# Revit family: Facade_60_Curtain_Wall_S13_Standard
name_source: partatom
category: Windows
revit_build: Autodesk Revit 2014 (Build: 20130308_1515(x64)
units: mm (PartAtom-declared; Revit-internal decimal feet)

## types (72) — shared parameters
100mm Mullion = Yes
160mm Mullion = No
190mm Mullion = No
Custom Offset From Exterior = 10 mm  [stored 0.0328084 ft]
DG Gasket Thickness = 12 mm  [stored 0.0393701 ft]
Description = Curtain wall, S13
Frame Bottom Gap = 30 mm  [stored 0.0984252 ft]
Frame Thickness = 102 mm
Glazing Bottom Gap = 70 mm
Glazing Side Gap = 40 mm  [stored 0.131234 ft]
Glazing Top Gap = 40 mm  [stored 0.131234 ft]
Half Expansion Break = No
Jamb Width = 60 mm  [stored 0.19685 ft]
Limit Door Height Max = 18149 mm
Limit Door Height Min = 1049 mm
Limit Door Width Max = 3080 mm
Limit Door Width Min = 380 mm
Limit Panel Height Max = 6000 mm  [stored 19.685 ft]
Limit Panel Height Min = 300 mm  [stored 0.984252 ft]
Limit Panel Width Max = 3000 mm  [stored 9.84252 ft]
Limit Panel Width Min = 300 mm  [stored 0.984252 ft]
Manufacturer = Crealco
Max System DG Unit Thickness = 25 mm  [stored 0.082021 ft]
Model = Façade 60
Mullion Configuration = 1 mm  [stored 0.00328084 ft]
Quarter Expansion Break = No
Sill Height = 85 mm  [stored 0.278871 ft]
Thermal Break Material = Plastic, Opaque Black
URL = http://www.crealco.co.za
Wall Closure = By host
zero-valued in all types: Default Sill Height

## per-type parameters (varying)
| type | Custom Curtain Wall Height | Custom Curtain Wall Width | Custom Windload | Intruderprufe Insulated LowE SHGC Value | Intruderprufe Insulated LowE U Value | Intruderprufe Insulated SHGC Value | Intruderprufe Insulated U Value | Intruderprufe LowE SHGC Value | Intruderprufe LowE U Value | Intruderprufe SHGC Value | Intruderprufe U Value |
| F60-S13-0925-1000Pa | 2490 mm | 890 mm  [stored 2.91995 ft] | 1000 mm  [stored 3.28084 ft] | 0.491 | 2.76 | 0.544 | 3.31 | 0.553 | 4.63 | 0.63 | 5.75 |
| F60-S13-0925-1500Pa | 2490 mm | 890 mm  [stored 2.91995 ft] | 1500 mm  [stored 4.92126 ft] | 0.491 | 2.76 | 0.544 | 3.31 | 0.553 | 4.63 | 0.63 | 5.75 |
| F60-S13-0925-2000Pa | 2490 mm | 890 mm  [stored 2.91995 ft] | 2000 mm  [stored 6.56168 ft] | 0.491 | 2.76 | 0.544 | 3.31 | 0.553 | 4.63 | 0.63 | 5.75 |
| F60-S13-1225-1000Pa | 2490 mm | 1190 mm  [stored 3.9042 ft] | 1000 mm  [stored 3.28084 ft] | 0.508 | 2.65 | 0.564 | 3.23 | 0.573 | 4.52 | 0.653 | 5.76 |
| F60-S13-1225-1500Pa | 2490 mm | 1190 mm  [stored 3.9042 ft] | 1500 mm  [stored 4.92126 ft] | 0.508 | 2.65 | 0.564 | 3.23 | 0.573 | 4.52 | 0.653 | 5.76 |
| F60-S13-1225-2000Pa | 2490 mm | 1190 mm  [stored 3.9042 ft] | 2000 mm  [stored 6.56168 ft] | 0.508 | 2.65 | 0.564 | 3.23 | 0.573 | 4.52 | 0.653 | 5.76 |
| F60-S13-1525-1000Pa | 2490 mm | 1490 mm  [stored 4.88845 ft] | 1000 mm  [stored 3.28084 ft] | 0.519 | 2.58 | 0.575 | 3.18 | 0.585 | 4.46 | 0.667 | 5.76 |
| F60-S13-1525-1500Pa | 2490 mm | 1490 mm  [stored 4.88845 ft] | 1500 mm  [stored 4.92126 ft] | 0.519 | 2.58 | 0.575 | 3.18 | 0.585 | 4.46 | 0.667 | 5.76 |
| F60-S13-1525-2000Pa | 2490 mm | 1490 mm  [stored 4.88845 ft] | 2000 mm  [stored 6.56168 ft] | 0.519 | 2.58 | 0.575 | 3.18 | 0.585 | 4.46 | 0.667 | 5.76 |
| F60-S13-1825-1000Pa | 2490 mm | 1790 mm  [stored 5.8727 ft] | 1000 mm  [stored 3.28084 ft] | 0.526 | 2.54 | 0.583 | 3.15 | 0.593 | 4.42 | 0.676 | 5.77 |
| F60-S13-1825-1500Pa | 2490 mm | 1790 mm  [stored 5.8727 ft] | 1500 mm  [stored 4.92126 ft] | 0.526 | 2.54 | 0.583 | 3.15 | 0.593 | 4.42 | 0.676 | 5.77 |
| F60-S13-1825-2000Pa | 2490 mm | 1790 mm  [stored 5.8727 ft] | 2000 mm  [stored 6.56168 ft] | 0.526 | 2.54 | 0.583 | 3.15 | 0.593 | 4.42 | 0.676 | 5.77 |
| F60-S13-2125-1000Pa | 2490 mm | 2090 mm  [stored 6.85696 ft] | 1000 mm  [stored 3.28084 ft] | 0.531 | 2.5 | 0.588 | 3.12 | 0.598 | 4.39 | 0.683 | 5.77 |
| F60-S13-2125-1500Pa | 2490 mm | 2090 mm  [stored 6.85696 ft] | 1500 mm  [stored 4.92126 ft] | 0.531 | 2.5 | 0.588 | 3.12 | 0.598 | 4.39 | 0.683 | 5.77 |
| F60-S13-2125-2000Pa | 2490 mm | 2090 mm  [stored 6.85696 ft] | 2000 mm  [stored 6.56168 ft] | 0.531 | 2.5 | 0.588 | 3.12 | 0.598 | 4.39 | 0.683 | 5.77 |
| F60-S13-2425-1000Pa | 2490 mm | 2390 mm  [stored 7.84121 ft] | 1000 mm  [stored 3.28084 ft] | 0.534 | 2.48 | 0.593 | 3.11 | 0.603 | 4.37 | 0.688 | 5.77 |
| F60-S13-2425-1500Pa | 2490 mm | 2390 mm  [stored 7.84121 ft] | 1500 mm  [stored 4.92126 ft] | 0.534 | 2.48 | 0.593 | 3.11 | 0.603 | 4.37 | 0.688 | 5.77 |
| F60-S13-2425-2000Pa | 2490 mm | 2390 mm  [stored 7.84121 ft] | 2000 mm  [stored 6.56168 ft] | 0.534 | 2.48 | 0.593 | 3.11 | 0.603 | 4.37 | 0.688 | 5.77 |
| F60-S13-2725-1000Pa | 2490 mm | 2690 mm | 1000 mm  [stored 3.28084 ft] | 0.537 | 2.46 | 0.596 | 3.09 | 0.606 | 4.36 | 0.692 | 5.77 |
| F60-S13-2725-1500Pa | 2490 mm | 2690 mm | 1500 mm  [stored 4.92126 ft] | 0.537 | 2.46 | 0.596 | 3.09 | 0.606 | 4.36 | 0.692 | 5.77 |
| F60-S13-2725-2000Pa | 2490 mm | 2690 mm | 2000 mm  [stored 6.56168 ft] | 0.537 | 2.46 | 0.596 | 3.09 | 0.606 | 4.36 | 0.692 | 5.77 |
| F60-S13-3025-1000Pa | 2490 mm | 2990 mm  [stored 9.80971 ft] | 1000 mm  [stored 3.28084 ft] | 0.539 | 2.45 | 0.598 | 3.08 | 0.609 | 4.34 | 0.695 | 5.77 |
| F60-S13-3025-1500Pa | 2490 mm | 2990 mm  [stored 9.80971 ft] | 1500 mm  [stored 4.92126 ft] | 0.539 | 2.45 | 0.598 | 3.08 | 0.609 | 4.34 | 0.695 | 5.77 |
| F60-S13-3025-2000Pa | 2490 mm | 2990 mm  [stored 9.80971 ft] | 2000 mm  [stored 6.56168 ft] | 0.539 | 2.45 | 0.598 | 3.08 | 0.609 | 4.34 | 0.695 | 5.77 |
| F60-S13-0950-1000Pa | 4990 mm  [stored 16.3714 ft] | 890 mm  [stored 2.91995 ft] | 1000 mm  [stored 3.28084 ft] | 0.518 | 2.58 | 0.574 | 3.18 | 0.584 | 4.4 | 0.666 | 5.73 |
| F60-S13-0950-1500Pa | 4990 mm  [stored 16.3714 ft] | 890 mm  [stored 2.91995 ft] | 1500 mm  [stored 4.92126 ft] | 0.518 | 2.58 | 0.574 | 3.18 | 0.584 | 4.4 | 0.666 | 5.73 |
| F60-S13-0950-2000Pa | 4990 mm  [stored 16.3714 ft] | 890 mm  [stored 2.91995 ft] | 2000 mm  [stored 6.56168 ft] | 0.518 | 2.58 | 0.574 | 3.18 | 0.584 | 4.4 | 0.666 | 5.73 |
| F60-S13-1250-1000Pa | 4990 mm  [stored 16.3714 ft] | 1190 mm  [stored 3.9042 ft] | 1000 mm  [stored 3.28084 ft] | 0.536 | 2.46 | 0.595 | 3.09 | 0.605 | 4.28 | 0.691 | 5.74 |
| F60-S13-1250-1500Pa | 4990 mm  [stored 16.3714 ft] | 1190 mm  [stored 3.9042 ft] | 1500 mm  [stored 4.92126 ft] | 0.536 | 2.46 | 0.595 | 3.09 | 0.605 | 4.28 | 0.691 | 5.74 |
| F60-S13-1250-2000Pa | 4990 mm  [stored 16.3714 ft] | 1190 mm  [stored 3.9042 ft] | 2000 mm  [stored 6.56168 ft] | 0.536 | 2.46 | 0.595 | 3.09 | 0.605 | 4.28 | 0.691 | 5.74 |
| F60-S13-1550-1000Pa | 4990 mm  [stored 16.3714 ft] | 1490 mm  [stored 4.88845 ft] | 1000 mm  [stored 3.28084 ft] | 0.547 | 2.38 | 0.607 | 3.04 | 0.618 | 4.21 | 0.706 | 5.75 |
| F60-S13-1550-1500Pa | 4990 mm  [stored 16.3714 ft] | 1490 mm  [stored 4.88845 ft] | 1500 mm  [stored 4.92126 ft] | 0.547 | 2.38 | 0.607 | 3.04 | 0.618 | 4.21 | 0.706 | 5.75 |
| F60-S13-1550-2000Pa | 4990 mm  [stored 16.3714 ft] | 1490 mm  [stored 4.88845 ft] | 2000 mm  [stored 6.56168 ft] | 0.547 | 2.38 | 0.607 | 3.04 | 0.618 | 4.21 | 0.706 | 5.75 |
| F60-S13-1850-1000Pa | 4990 mm  [stored 16.3714 ft] | 1790 mm  [stored 5.8727 ft] | 1000 mm  [stored 3.28084 ft] | 0.547 | 2.38 | 0.607 | 3.04 | 0.618 | 4.21 | 0.706 | 5.75 |
| F60-S13-1850-1500Pa | 4990 mm  [stored 16.3714 ft] | 1790 mm  [stored 5.8727 ft] | 1500 mm  [stored 4.92126 ft] | 0.547 | 2.38 | 0.607 | 3.04 | 0.618 | 4.21 | 0.706 | 5.75 |
| F60-S13-1850-2000Pa | 4990 mm  [stored 16.3714 ft] | 1790 mm  [stored 5.8727 ft] | 2000 mm  [stored 6.56168 ft] | 0.547 | 2.38 | 0.607 | 3.04 | 0.618 | 4.21 | 0.706 | 5.75 |
| F60-S13-2150-1000Pa | 4990 mm  [stored 16.3714 ft] | 2090 mm  [stored 6.85696 ft] | 1000 mm  [stored 3.28084 ft] | 0.56 | 2.3 | 0.621 | 2.98 | 0.633 | 4.13 | 0.722 | 5.75 |
| F60-S13-2150-1500Pa | 4990 mm  [stored 16.3714 ft] | 2090 mm  [stored 6.85696 ft] | 1500 mm  [stored 4.92126 ft] | 0.56 | 2.3 | 0.621 | 2.98 | 0.633 | 4.13 | 0.722 | 5.75 |
| F60-S13-2150-2000Pa | 4990 mm  [stored 16.3714 ft] | 2090 mm  [stored 6.85696 ft] | 2000 mm  [stored 6.56168 ft] | 0.56 | 2.3 | 0.621 | 2.98 | 0.633 | 4.13 | 0.722 | 5.75 |
| F60-S13-2450-1000Pa | 4990 mm  [stored 16.3714 ft] | 2390 mm  [stored 7.84121 ft] | 1000 mm  [stored 3.28084 ft] | 0.564 | 2.29 | 0.626 | 2.96 | 0.637 | 4.1 | 0.728 | 5.75 |
| F60-S13-2450-1500Pa | 4990 mm  [stored 16.3714 ft] | 2390 mm  [stored 7.84121 ft] | 1500 mm  [stored 4.92126 ft] | 0.564 | 2.29 | 0.626 | 2.96 | 0.637 | 4.1 | 0.728 | 5.75 |
| F60-S13-2450-2000Pa | 4990 mm  [stored 16.3714 ft] | 2390 mm  [stored 7.84121 ft] | 2000 mm  [stored 6.56168 ft] | 0.564 | 2.29 | 0.626 | 2.96 | 0.637 | 4.1 | 0.728 | 5.75 |
| F60-S13-2750-1000Pa | 4990 mm  [stored 16.3714 ft] | 2690 mm | 1000 mm  [stored 3.28084 ft] | 0.567 | 2.26 | 0.629 | 2.94 | 0.641 | 4.08 | 0.732 | 5.75 |
| F60-S13-2750-1500Pa | 4990 mm  [stored 16.3714 ft] | 2690 mm | 1500 mm  [stored 4.92126 ft] | 0.567 | 2.26 | 0.629 | 2.94 | 0.641 | 4.08 | 0.732 | 5.75 |
| F60-S13-2750-2000Pa | 4990 mm  [stored 16.3714 ft] | 2690 mm | 2000 mm  [stored 6.56168 ft] | 0.567 | 2.26 | 0.629 | 2.94 | 0.641 | 4.08 | 0.732 | 5.75 |
| F60-S13-3050-1000Pa | 4990 mm  [stored 16.3714 ft] | 2990 mm  [stored 9.80971 ft] | 1000 mm  [stored 3.28084 ft] | 0.569 | 2.24 | 0.632 | 2.93 | 0.644 | 4.07 | 0.735 | 5.76 |
| F60-S13-3050-1500Pa | 4990 mm  [stored 16.3714 ft] | 2990 mm  [stored 9.80971 ft] | 1500 mm  [stored 4.92126 ft] | 0.569 | 2.24 | 0.632 | 2.93 | 0.644 | 4.07 | 0.735 | 5.76 |
| F60-S13-3050-2000Pa | 4990 mm  [stored 16.3714 ft] | 2990 mm  [stored 9.80971 ft] | 2000 mm  [stored 6.56168 ft] | 0.569 | 2.24 | 0.632 | 2.93 | 0.644 | 4.07 | 0.735 | 5.76 |
| F60-S13-0975-1000Pa | 7490 mm | 890 mm  [stored 2.91995 ft] | 1000 mm  [stored 3.28084 ft] | 0.527 | 2.52 | 0.585 | 3.13 | 0.594 | 4.33 | 0.678 | 5.72 |
| F60-S13-0975-1500Pa | 7490 mm | 890 mm  [stored 2.91995 ft] | 1500 mm  [stored 4.92126 ft] | 0.527 | 2.52 | 0.585 | 3.13 | 0.594 | 4.33 | 0.678 | 5.72 |
| F60-S13-0975-2000Pa | 7490 mm | 890 mm  [stored 2.91995 ft] | 2000 mm  [stored 6.56168 ft] | 0.527 | 2.52 | 0.585 | 3.13 | 0.594 | 4.33 | 0.678 | 5.72 |
| F60-S13-1275-1000Pa | 7490 mm | 1190 mm  [stored 3.9042 ft] | 1000 mm  [stored 3.28084 ft] | 0.546 | 2.39 | 0.606 | 3.04 | 0.616 | 4.2 | 0.703 | 5.73 |
| F60-S13-1275-1500Pa | 7490 mm | 1190 mm  [stored 3.9042 ft] | 1500 mm  [stored 4.92126 ft] | 0.546 | 2.39 | 0.606 | 3.04 | 0.616 | 4.2 | 0.703 | 5.73 |
| F60-S13-1275-2000Pa | 7490 mm | 1190 mm  [stored 3.9042 ft] | 2000 mm  [stored 6.56168 ft] | 0.546 | 2.39 | 0.606 | 3.04 | 0.616 | 4.2 | 0.703 | 5.73 |
| F60-S13-1575-1000Pa | 7490 mm | 1490 mm  [stored 4.88845 ft] | 1000 mm  [stored 3.28084 ft] | 0.557 | 2.32 | 0.618 | 2.99 | 0.629 | 4.13 | 0.718 | 5.74 |
| F60-S13-1575-1500Pa | 7490 mm | 1490 mm  [stored 4.88845 ft] | 1500 mm  [stored 4.92126 ft] | 0.557 | 2.32 | 0.618 | 2.99 | 0.629 | 4.13 | 0.718 | 5.74 |
| F60-S13-1575-2000Pa | 7490 mm | 1490 mm  [stored 4.88845 ft] | 2000 mm  [stored 6.56168 ft] | 0.557 | 2.32 | 0.618 | 2.99 | 0.629 | 4.13 | 0.718 | 5.74 |
| F60-S13-1875-1000Pa | 7490 mm | 1790 mm  [stored 5.8727 ft] | 1000 mm  [stored 3.28084 ft] | 0.564 | 2.27 | 0.626 | 2.95 | 0.638 | 4.08 | 0.728 | 5.74 |
| F60-S13-1875-1500Pa | 7490 mm | 1790 mm  [stored 5.8727 ft] | 1500 mm  [stored 4.92126 ft] | 0.564 | 2.27 | 0.626 | 2.95 | 0.638 | 4.08 | 0.728 | 5.74 |
| F60-S13-1875-2000Pa | 7490 mm | 1790 mm  [stored 5.8727 ft] | 2000 mm  [stored 6.56168 ft] | 0.564 | 2.27 | 0.626 | 2.95 | 0.638 | 4.08 | 0.728 | 5.74 |
| F60-S13-2175-1000Pa | 7490 mm | 2090 mm  [stored 6.85696 ft] | 1000 mm  [stored 3.28084 ft] | 0.57 | 2.23 | 0.632 | 2.93 | 0.644 | 4.04 | 0.736 | 5.74 |
| F60-S13-2175-1500Pa | 7490 mm | 2090 mm  [stored 6.85696 ft] | 1500 mm  [stored 4.92126 ft] | 0.57 | 2.23 | 0.632 | 2.93 | 0.644 | 4.04 | 0.736 | 5.74 |
| F60-S13-2175-2000Pa | 7490 mm | 2090 mm  [stored 6.85696 ft] | 2000 mm  [stored 6.56168 ft] | 0.57 | 2.23 | 0.632 | 2.93 | 0.644 | 4.04 | 0.736 | 5.74 |
| F60-S13-2475-1000Pa | 7490 mm | 2390 mm  [stored 7.84121 ft] | 1000 mm  [stored 3.28084 ft] | 0.574 | 2.21 | 0.637 | 2.91 | 0.649 | 4.01 | 0.741 | 5.75 |
| F60-S13-2475-1500Pa | 7490 mm | 2390 mm  [stored 7.84121 ft] | 1500 mm  [stored 4.92126 ft] | 0.574 | 2.21 | 0.637 | 2.91 | 0.649 | 4.01 | 0.741 | 5.75 |
| F60-S13-2475-2000Pa | 7490 mm | 2390 mm  [stored 7.84121 ft] | 2000 mm  [stored 6.56168 ft] | 0.574 | 2.21 | 0.637 | 2.91 | 0.649 | 4.01 | 0.741 | 5.75 |
| F60-S13-2775-1000Pa | 7490 mm | 2690 mm | 1000 mm  [stored 3.28084 ft] | 0.577 | 2.19 | 0.64 | 2.89 | 0.652 | 3.99 | 0.745 | 5.75 |
| F60-S13-2775-1500Pa | 7490 mm | 2690 mm | 1500 mm  [stored 4.92126 ft] | 0.577 | 2.19 | 0.64 | 2.89 | 0.652 | 3.99 | 0.745 | 5.75 |
| F60-S13-2775-2000Pa | 7490 mm | 2690 mm | 2000 mm  [stored 6.56168 ft] | 0.577 | 2.19 | 0.64 | 2.89 | 0.652 | 3.99 | 0.745 | 5.75 |
| F60-S13-3075-1000Pa | 7490 mm | 2990 mm  [stored 9.80971 ft] | 1000 mm  [stored 3.28084 ft] | 0.579 | 2.17 | 0.643 | 2.88 | 0.655 | 3.98 | 0.748 | 5.75 |
| F60-S13-3075-1500Pa | 7490 mm | 2990 mm  [stored 9.80971 ft] | 1500 mm  [stored 4.92126 ft] | 0.579 | 2.17 | 0.643 | 2.88 | 0.655 | 3.98 | 0.748 | 5.75 |
| F60-S13-3075-2000Pa | 7490 mm | 2990 mm  [stored 9.80971 ft] | 2000 mm  [stored 6.56168 ft] | 0.579 | 2.17 | 0.643 | 2.88 | 0.655 | 3.98 | 0.748 | 5.75 |

note: [stored X ft] marks values corroborated as IEEE doubles in the binary element streams (Revit-internal decimal feet)

## geometry (parser evidence)
native form markers: Sweep x17
no freeform markers — native parametric forms only
